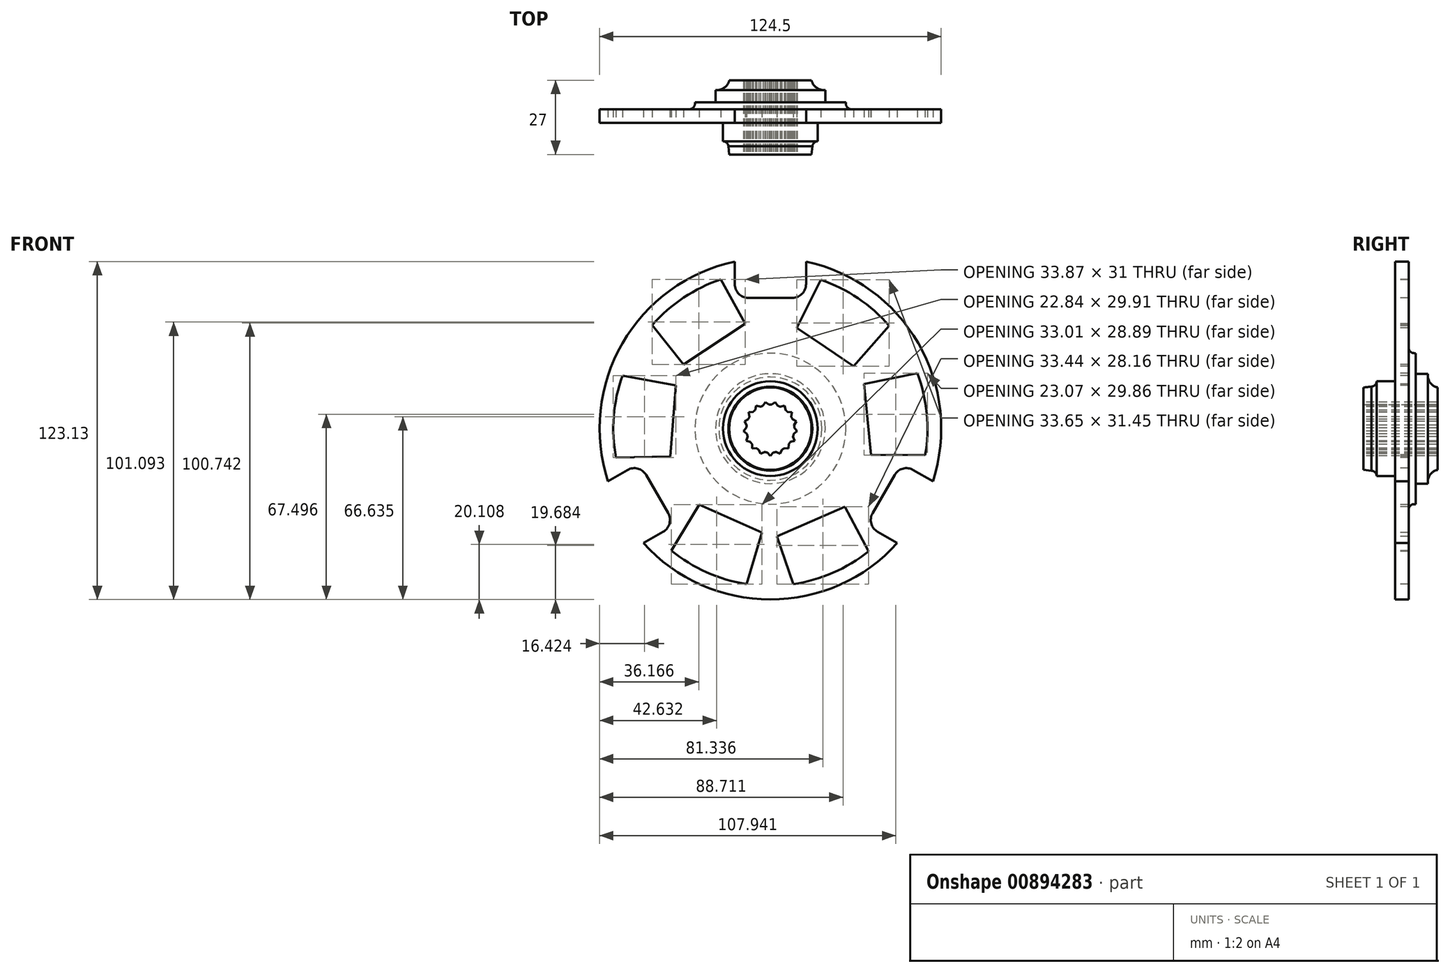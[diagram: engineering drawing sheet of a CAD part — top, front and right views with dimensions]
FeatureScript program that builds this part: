
annotation { "Feature Type Name" : "Feature", "Feature Type Description" : "" }
export const myFeature = defineFeature(function(context is Context, id is Id, definition is map)
    precondition{}
    {
        {
            var Q0;
            Q0=qCreatedBy(makeId("Right.planeOp"),FACE);
            var sketch = newSketch(context, id + "F0", { "sketchPlane" : qUnion([Q0])});
            skLineSegment(sketch, "E0", {"start": v(27, 8.75) * mm, "end": v(27, 15) * mm});
            skLineSegment(sketch, "E1", {"start": v(23.5, 20) * mm, "end": v(19, 20) * mm});
            skLineSegment(sketch, "E2", {"start": v(19, 20) * mm, "end": v(19, 27.5) * mm});
            skLineSegment(sketch, "E3", {"start": v(19, 27.5) * mm, "end": v(18.5, 27.5) * mm});
            skLineSegment(sketch, "E4", {"start": v(16.5, 29.5) * mm, "end": v(16.5, 62.25) * mm});
            skArc(sketch, "E5", {"start": v(16.5, 29.5) * mm, "mid": v(17.09, 28.09) * mm, "end": v(18.5, 27.5) * mm});
            skLineSegment(sketch, "E6", {"start": v(16.5, 62.25) * mm, "end": v(11.5, 62.25) * mm});
            skLineSegment(sketch, "E7", {"start": v(11.5, 62.25) * mm, "end": v(11.5, 17.25) * mm});
            skLineSegment(sketch, "E8", {"start": v(11.5, 17.25) * mm, "end": v(4.8, 17.25) * mm});
            skLineSegment(sketch, "E9", {"start": v(27, 0) * mm, "end": v(0, 0) * mm});
            skLineSegment(sketch, "E10", {"start": v(0, 8.75) * mm, "end": v(0, 15) * mm});
            skLineSegment(sketch, "E11", {"start": v(0, 8.75) * mm, "end": v(27, 8.75) * mm});
            skArc(sketch, "E12", {"start": v(23.5, 18.8) * mm, "mid": v(24.65, 16.34) * mm, "end": v(27, 15) * mm});
            skLineSegment(sketch, "E13", {"start": v(0, 15) * mm, "end": v(2.96, 15.3) * mm});
            skArc(sketch, "E14", {"start": v(2.96, 15.3) * mm, "mid": v(4.25, 15.92) * mm, "end": v(4.8, 17.25) * mm});
            skLineSegment(sketch, "E15", {"start": v(0, 0) * mm, "end": v(0, 8.75) * mm, "construction": true});
            skLineSegment(sketch, "E16", {"start": v(23.5, 20) * mm, "end": v(23.5, 18.8) * mm});
            skSolve(sketch);
        }
        {
            var Q0;
            Q0=makeQuery(id+"F0.imprint","IMPRINT",FACE,{"disambiguationData":[TD([[makeQuery(id+"F0.imprint","IMPRINT",EDGE,{"derivedFrom":sQuery(id+"F0.wireOp",EDGE,"E0")}),1.0]])]});
            var Q1;
            Q1=sQuery(id+"F0.wireOp",EDGE,"E9");
            revolve(context, id + "F1", {"surfaceOperationType" : NewSurfaceOperationType.NEW, "entities" : qUnion([Q0]), "axis" : qUnion([Q1]), "revolveType" : RevolveType.FULL});
        }
        {
            var Q0;
            Q0=makeQuery(id+"F1.opRevolve","SWEPT_FACE",FACE,{"disambiguationData":[OSD([sQuery(id+"F0.wireOp",EDGE,"E10")])]});
            var sketch = newSketch(context, id + "F2", { "sketchPlane" : qUnion([Q0])});
            skArc(sketch, "E17", {"start": v(0.5, 8.74) * mm, "mid": v(0, 8.75) * mm, "end": v(-0.5, 8.74) * mm});
            skArc(sketch, "E18", {"start": v(-2.69, 8.33) * mm, "mid": v(-3.16, 8.16) * mm, "end": v(-3.62, 7.97) * mm});
            skArc(sketch, "E19", {"start": v(-5.52, 6.8) * mm, "mid": v(-5.9, 6.47) * mm, "end": v(-6.25, 6.12) * mm});
            skArc(sketch, "E20", {"start": v(-7.6, 4.34) * mm, "mid": v(-7.83, 3.9) * mm, "end": v(-8.04, 3.45) * mm});
            skArc(sketch, "E21", {"start": v(-8.65, 1.3) * mm, "mid": v(-8.71, 0.8) * mm, "end": v(-8.74, 0.3) * mm});
            skArc(sketch, "E22", {"start": v(-8.54, -1.9) * mm, "mid": v(-8.42, -2.4) * mm, "end": v(-8.27, -2.87) * mm});
            skArc(sketch, "E23", {"start": v(-7.27, -4.87) * mm, "mid": v(-6.98, -5.27) * mm, "end": v(-6.67, -5.66) * mm});
            skArc(sketch, "E24", {"start": v(-5.02, -7.16) * mm, "mid": v(-4.6, -7.44) * mm, "end": v(-4.17, -7.7) * mm});
            skArc(sketch, "E25", {"start": v(-2.1, -8.5) * mm, "mid": v(-1.6, -8.6) * mm, "end": v(-1.11, -8.68) * mm});
            skArc(sketch, "E26", {"start": v(1.11, -8.68) * mm, "mid": v(1.6, -8.6) * mm, "end": v(2.1, -8.5) * mm});
            skArc(sketch, "E27", {"start": v(4.17, -7.7) * mm, "mid": v(4.6, -7.44) * mm, "end": v(5.02, -7.16) * mm});
            skArc(sketch, "E28", {"start": v(6.67, -5.66) * mm, "mid": v(6.98, -5.27) * mm, "end": v(7.27, -4.87) * mm});
            skArc(sketch, "E29", {"start": v(8.27, -2.87) * mm, "mid": v(8.42, -2.4) * mm, "end": v(8.54, -1.9) * mm});
            skArc(sketch, "E30", {"start": v(8.74, 0.3) * mm, "mid": v(8.71, 0.8) * mm, "end": v(8.65, 1.3) * mm});
            skArc(sketch, "E31", {"start": v(8.04, 3.45) * mm, "mid": v(7.83, 3.9) * mm, "end": v(7.6, 4.34) * mm});
            skArc(sketch, "E32", {"start": v(6.25, 6.12) * mm, "mid": v(5.9, 6.47) * mm, "end": v(5.52, 6.8) * mm});
            skArc(sketch, "E33", {"start": v(3.62, 7.97) * mm, "mid": v(3.16, 8.16) * mm, "end": v(2.69, 8.33) * mm});
            skLineSegment(sketch, "E34", {"start": v(0.5, 8.74) * mm, "end": v(1.8, 9.68) * mm});
            skLineSegment(sketch, "E35", {"start": v(1.8, 9.68) * mm, "end": v(2.69, 8.33) * mm});
            skLineSegment(sketch, "E36", {"start": v(-2.69, 8.33) * mm, "end": v(-1.8, 9.68) * mm});
            skLineSegment(sketch, "E37", {"start": v(-1.8, 9.68) * mm, "end": v(-0.5, 8.74) * mm});
            skLineSegment(sketch, "E38", {"start": v(-5.52, 6.8) * mm, "end": v(-5.19, 8.37) * mm});
            skLineSegment(sketch, "E39", {"start": v(-5.19, 8.37) * mm, "end": v(-3.62, 7.97) * mm});
            skLineSegment(sketch, "E40", {"start": v(-7.6, 4.34) * mm, "end": v(-7.86, 5.94) * mm});
            skLineSegment(sketch, "E41", {"start": v(-7.86, 5.94) * mm, "end": v(-6.25, 6.12) * mm});
            skLineSegment(sketch, "E42", {"start": v(-8.65, 1.3) * mm, "end": v(-9.47, 2.7) * mm});
            skLineSegment(sketch, "E43", {"start": v(-9.47, 2.7) * mm, "end": v(-8.04, 3.45) * mm});
            skLineSegment(sketch, "E44", {"start": v(-8.54, -1.9) * mm, "end": v(-9.8, -0.9) * mm});
            skLineSegment(sketch, "E45", {"start": v(-9.8, -0.9) * mm, "end": v(-8.74, 0.3) * mm});
            skLineSegment(sketch, "E46", {"start": v(-7.27, -4.87) * mm, "end": v(-8.82, -4.4) * mm});
            skLineSegment(sketch, "E47", {"start": v(-8.82, -4.4) * mm, "end": v(-8.27, -2.87) * mm});
            skLineSegment(sketch, "E48", {"start": v(-5.02, -7.16) * mm, "end": v(-6.64, -7.28) * mm});
            skLineSegment(sketch, "E49", {"start": v(-6.64, -7.28) * mm, "end": v(-6.67, -5.66) * mm});
            skLineSegment(sketch, "E50", {"start": v(-2.1, -8.5) * mm, "end": v(-3.56, -9.18) * mm});
            skLineSegment(sketch, "E51", {"start": v(-3.56, -9.18) * mm, "end": v(-4.17, -7.7) * mm});
            skLineSegment(sketch, "E52", {"start": v(1.11, -8.68) * mm, "end": v(0, -9.85) * mm});
            skLineSegment(sketch, "E53", {"start": v(0, -9.85) * mm, "end": v(-1.11, -8.68) * mm});
            skLineSegment(sketch, "E54", {"start": v(4.17, -7.7) * mm, "end": v(3.56, -9.18) * mm});
            skLineSegment(sketch, "E55", {"start": v(3.56, -9.18) * mm, "end": v(2.1, -8.5) * mm});
            skLineSegment(sketch, "E56", {"start": v(6.67, -5.66) * mm, "end": v(6.64, -7.28) * mm});
            skLineSegment(sketch, "E57", {"start": v(6.64, -7.28) * mm, "end": v(5.02, -7.16) * mm});
            skLineSegment(sketch, "E58", {"start": v(8.27, -2.87) * mm, "end": v(8.82, -4.4) * mm});
            skLineSegment(sketch, "E59", {"start": v(8.82, -4.4) * mm, "end": v(7.27, -4.87) * mm});
            skLineSegment(sketch, "E60", {"start": v(8.74, 0.3) * mm, "end": v(9.8, -0.9) * mm});
            skLineSegment(sketch, "E61", {"start": v(9.8, -0.9) * mm, "end": v(8.54, -1.9) * mm});
            skLineSegment(sketch, "E62", {"start": v(8.04, 3.45) * mm, "end": v(9.47, 2.7) * mm});
            skLineSegment(sketch, "E63", {"start": v(9.47, 2.7) * mm, "end": v(8.65, 1.3) * mm});
            skLineSegment(sketch, "E64", {"start": v(6.25, 6.12) * mm, "end": v(7.86, 5.94) * mm});
            skLineSegment(sketch, "E65", {"start": v(7.86, 5.94) * mm, "end": v(7.6, 4.34) * mm});
            skLineSegment(sketch, "E66", {"start": v(3.62, 7.97) * mm, "end": v(5.19, 8.37) * mm});
            skLineSegment(sketch, "E67", {"start": v(5.19, 8.37) * mm, "end": v(5.52, 6.8) * mm});
            skArc(sketch, "E68", {"start": v(-18.01, 54.34) * mm, "mid": v(-31.62, 47.73) * mm, "end": v(-43.02, 37.77) * mm});
            skArc(sketch, "E69", {"start": v(-53.89, 19.34) * mm, "mid": v(-57.07, 4.54) * mm, "end": v(-56.27, -10.57) * mm});
            skArc(sketch, "E70", {"start": v(-36.12, -44.42) * mm, "mid": v(-23.22, -52.33) * mm, "end": v(-8.7, -56.59) * mm});
            skArc(sketch, "E71", {"start": v(8.3, -56.65) * mm, "mid": v(22.85, -52.5) * mm, "end": v(35.8, -44.67) * mm});
            skArc(sketch, "E72", {"start": v(56.42, -9.69) * mm, "mid": v(57, 5.44) * mm, "end": v(53.58, 20.18) * mm});
            skArc(sketch, "E73", {"start": v(43.28, 37.47) * mm, "mid": v(31.95, 47.5) * mm, "end": v(18.4, 54.22) * mm});
            skLineSegment(sketch, "E74", {"start": v(13, 60.88) * mm, "end": v(13, 52.65) * mm});
            skArc(sketch, "E75", {"start": v(8, 47.65) * mm, "mid": v(11.54, 49.11) * mm, "end": v(13, 52.65) * mm});
            skLineSegment(sketch, "E76", {"start": v(-13, 60.88) * mm, "end": v(-13, 52.65) * mm});
            skArc(sketch, "E77", {"start": v(-13, 52.65) * mm, "mid": v(-11.54, 49.11) * mm, "end": v(-8, 47.65) * mm});
            skLineSegment(sketch, "E78", {"start": v(-8, 47.65) * mm, "end": v(8, 47.65) * mm});
            skLineSegment(sketch, "E79", {"start": v(-59.22, -19.18) * mm, "end": v(-52.1, -15.07) * mm});
            skArc(sketch, "E80", {"start": v(-45.27, -16.9) * mm, "mid": v(-48.3, -14.57) * mm, "end": v(-52.1, -15.07) * mm});
            skLineSegment(sketch, "E81", {"start": v(-46.22, -41.7) * mm, "end": v(-39.1, -37.58) * mm});
            skArc(sketch, "E82", {"start": v(-39.1, -37.58) * mm, "mid": v(-36.77, -34.55) * mm, "end": v(-37.27, -30.75) * mm});
            skLineSegment(sketch, "E83", {"start": v(-37.27, -30.75) * mm, "end": v(-45.27, -16.9) * mm});
            skLineSegment(sketch, "E84", {"start": v(46.22, -41.7) * mm, "end": v(39.1, -37.58) * mm});
            skArc(sketch, "E85", {"start": v(37.27, -30.75) * mm, "mid": v(36.77, -34.55) * mm, "end": v(39.1, -37.58) * mm});
            skLineSegment(sketch, "E86", {"start": v(59.22, -19.18) * mm, "end": v(52.1, -15.07) * mm});
            skArc(sketch, "E87", {"start": v(52.1, -15.07) * mm, "mid": v(48.3, -14.57) * mm, "end": v(45.27, -16.9) * mm});
            skLineSegment(sketch, "E88", {"start": v(45.27, -16.9) * mm, "end": v(37.27, -30.75) * mm});
            skLineSegment(sketch, "E89", {"start": v(35.39, 3.38) * mm, "end": v(34.16, 16.32) * mm});
            skLineSegment(sketch, "E90", {"start": v(35.39, 3.38) * mm, "end": v(36.62, -9.57) * mm});
            skLineSegment(sketch, "E91", {"start": v(34.16, 16.32) * mm, "end": v(53.58, 20.18) * mm});
            skLineSegment(sketch, "E92", {"start": v(36.62, -9.57) * mm, "end": v(56.42, -9.69) * mm});
            skLineSegment(sketch, "E93", {"start": v(-35.44, 2.82) * mm, "end": v(-34.4, 15.78) * mm});
            skLineSegment(sketch, "E94", {"start": v(-35.44, 2.82) * mm, "end": v(-36.47, -10.14) * mm});
            skLineSegment(sketch, "E95", {"start": v(-56.27, -10.57) * mm, "end": v(-36.47, -10.14) * mm});
            skLineSegment(sketch, "E96", {"start": v(-34.4, 15.78) * mm, "end": v(-53.89, 19.34) * mm});
            skLineSegment(sketch, "E97", {"start": v(-20.4, 30.8) * mm, "end": v(-9.15, 38.26) * mm});
            skLineSegment(sketch, "E98", {"start": v(14.75, -33.88) * mm, "end": v(27.13, -28.49) * mm});
            skLineSegment(sketch, "E99", {"start": v(14.75, -33.88) * mm, "end": v(2.37, -39.27) * mm});
            skLineSegment(sketch, "E100", {"start": v(-43.02, 37.77) * mm, "end": v(-31.67, 23.34) * mm});
            skLineSegment(sketch, "E101", {"start": v(-9.15, 38.26) * mm, "end": v(-18.01, 54.34) * mm});
            skLineSegment(sketch, "E102", {"start": v(27.13, -28.49) * mm, "end": v(35.8, -44.67) * mm});
            skLineSegment(sketch, "E103", {"start": v(2.37, -39.27) * mm, "end": v(8.3, -56.65) * mm});
            skLineSegment(sketch, "E104", {"start": v(20.01, 29.75) * mm, "end": v(30.38, 22.77) * mm});
            skLineSegment(sketch, "E105", {"start": v(20.01, 29.75) * mm, "end": v(9.64, 36.72) * mm});
            skLineSegment(sketch, "E106", {"start": v(9.64, 36.72) * mm, "end": v(18.4, 54.22) * mm});
            skLineSegment(sketch, "E107", {"start": v(30.38, 22.77) * mm, "end": v(43.28, 37.47) * mm});
            skLineSegment(sketch, "E108", {"start": v(-14.54, -32.77) * mm, "end": v(-3.12, -37.84) * mm});
            skLineSegment(sketch, "E109", {"start": v(-14.54, -32.77) * mm, "end": v(-25.97, -27.7) * mm});
            skLineSegment(sketch, "E110", {"start": v(-25.97, -27.7) * mm, "end": v(-36.12, -44.42) * mm});
            skLineSegment(sketch, "E111", {"start": v(-3.12, -37.84) * mm, "end": v(-8.7, -56.59) * mm});
            skLineSegment(sketch, "E112", {"start": v(-20.4, 30.8) * mm, "end": v(-31.67, 23.34) * mm});
            skArc(sketch, "E113", {"start": v(13, 60.88) * mm, "mid": v(0, 62.25) * mm, "end": v(-13, 60.88) * mm});
            skArc(sketch, "E114", {"start": v(-59.22, -19.18) * mm, "mid": v(-53.91, -31.12) * mm, "end": v(-46.22, -41.7) * mm});
            skArc(sketch, "E115", {"start": v(46.22, -41.7) * mm, "mid": v(53.91, -31.12) * mm, "end": v(59.22, -19.18) * mm});
            skSolve(sketch);
        }
        {
            var Q0;
            Q0 = qSketchRegion(id + "F2", true);
            extrude(context, id + "F3", {"entities" : qUnion([Q0]), "operationType" : NewBodyOperationType.REMOVE, "endBound" : BoundingType.THROUGH_ALL, "oppositeDirection" : true, "depth" : 25 * mm, "offsetDistance" : 25 * mm});
        }
    });
